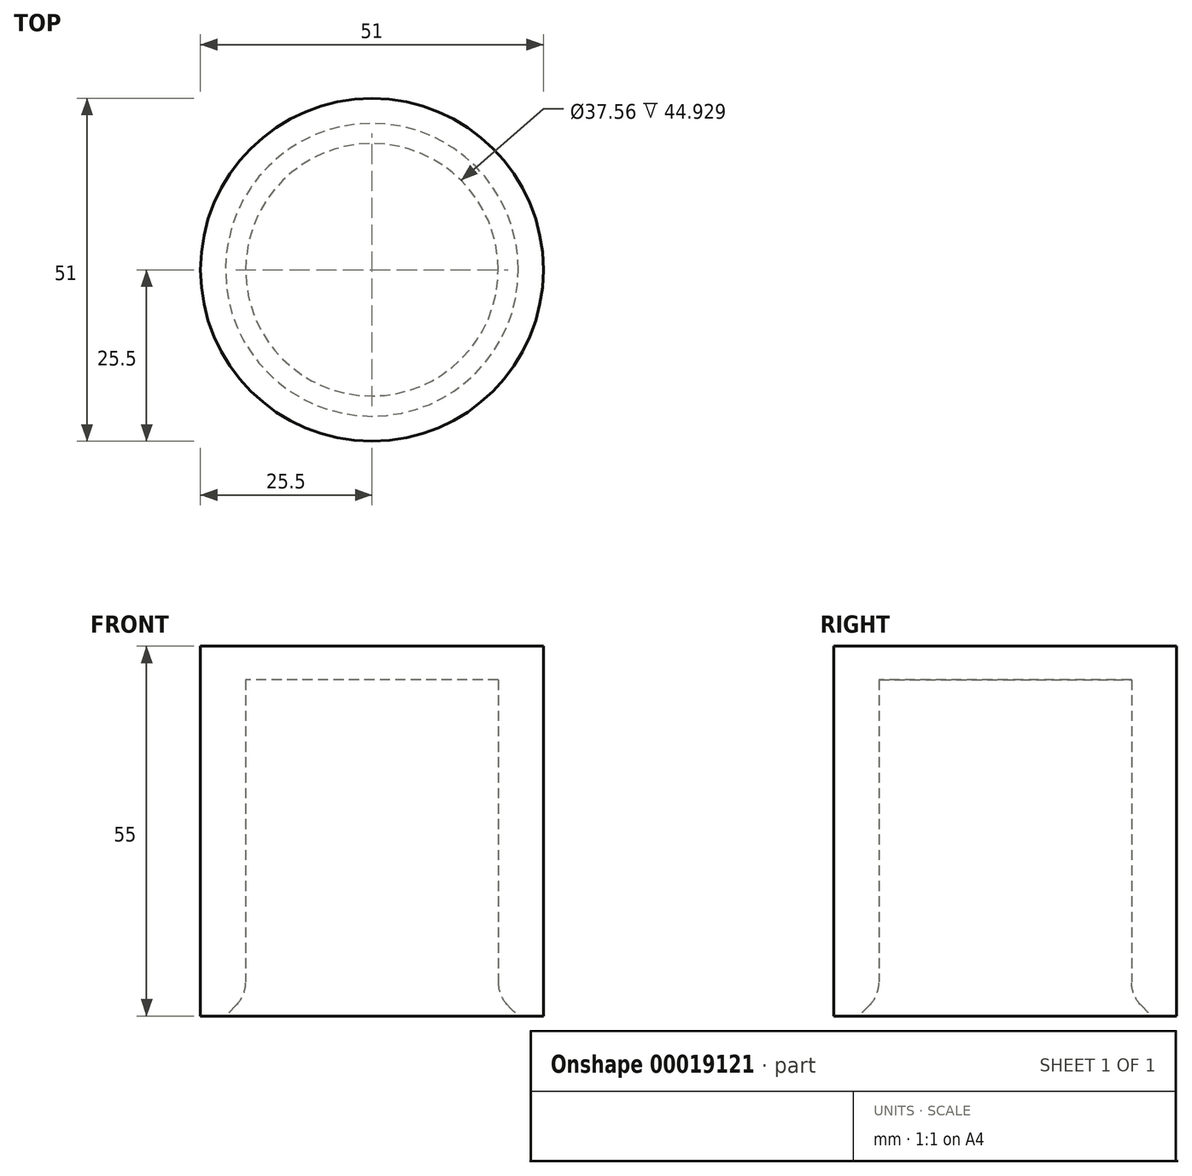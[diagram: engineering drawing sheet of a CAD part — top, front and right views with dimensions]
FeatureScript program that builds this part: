
annotation { "Feature Type Name" : "Feature", "Feature Type Description" : "" }
export const myFeature = defineFeature(function(context is Context, id is Id, definition is map)
    precondition{}
    {
        {
            var Q0;
            Q0=qCreatedBy(makeId("Top.planeOp"),FACE);
            var sketch = newSketch(context, id + "F0", { "sketchPlane" : qUnion([Q0])});
            skCircle(sketch, "E0", {"center": v(0, 0) * mm, "radius": 18.78 * mm});
            skCircle(sketch, "E1", {"center": v(0, 0) * mm, "radius": 25.5 * mm});
            skSolve(sketch);
        }
        {
            var Q0;
            Q0 = qSketchRegion(id + "F0", true);
            extrude(context, id + "F1", {"entities" : qUnion([Q0]), "depth" : 50 * mm});
        }
        {
            var Q0;
            Q0=makeQuery(id+"F1.opExtrude","CAP_FACE",FACE,{"disambiguationData":[OSD([sQuery(id+"F0.wireOp",EDGE,"E0"),sQuery(id+"F0.wireOp",EDGE,"E1")])],"isStart":false});
            var sketch = newSketch(context, id + "F2", { "sketchPlane" : qUnion([Q0])});
            skCircle(sketch, "E2.0", {"center": v(0, 0) * mm, "radius": 25.5 * mm});
            skSolve(sketch);
        }
        {
            var Q0;
            Q0 = qSketchRegion(id + "F2", true);
            extrude(context, id + "F3", {"entities" : qUnion([Q0]), "operationType" : NewBodyOperationType.ADD, "depth" : 5 * mm});
        }
        {
            var Q0;
            Q0=makeQuery(id+"F1.opExtrude","CAP_EDGE",EDGE,{"disambiguationData":[OSD([sQuery(id+"F0.wireOp",EDGE,"E0")])],"isStart":true});
            chamfer(context, id + "F4", {"entities" : qUnion([Q0]), "width" : 3 * mm, "tangentPropagation" : true});
        }
        {
            var Q0;
            {var subQ0=sQuery(id+"F0.wireOp",EDGE,"E0");Q0=makeQuery(id+"F4.opChamfer","BLEND_EDGE",EDGE,{"blendedFrom":[makeQuery(id+"F1.opExtrude","CAP_EDGE",EDGE,{"disambiguationData":[OSD([subQ0])],"isStart":true}),makeQuery(id+"F1.opExtrude","SWEPT_FACE",FACE,{"disambiguationData":[OSD([subQ0])]})],"blendedInto":[makeQuery(id+"F1.opExtrude","SWEPT_FACE",FACE,{"disambiguationData":[OSD([subQ0])]})]});}
            fillet(context, id + "F5", {"entities" : qUnion([Q0]), "radius" : 5 * mm, "tangentPropagation" : true, "allowEdgeOverflow" : false});
        }
    });
